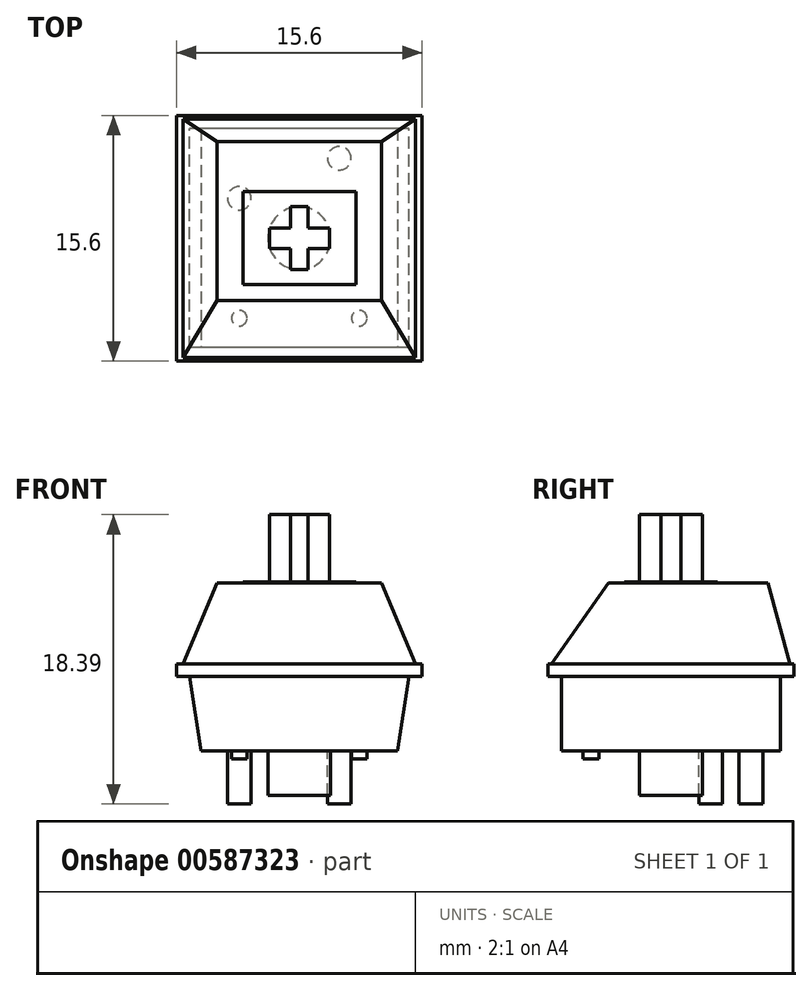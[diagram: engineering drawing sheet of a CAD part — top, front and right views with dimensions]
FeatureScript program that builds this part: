
annotation { "Feature Type Name" : "Feature", "Feature Type Description" : "" }
export const myFeature = defineFeature(function(context is Context, id is Id, definition is map)
    precondition{}
    {
        {
            var Q0;
            Q0=qCreatedBy(makeId("Top.planeOp"),FACE);
            var sketch = newSketch(context, id + "F0", { "sketchPlane" : qUnion([Q0])});
            skCircle(sketch, "E0", {"center": v(0, 0) * mm, "radius": 2 * mm});
            skCircle(sketch, "E1", {"center": v(-3.8, -5.08) * mm, "radius": 0.5 * mm});
            skCircle(sketch, "E2", {"center": v(3.81, -5.08) * mm, "radius": 0.5 * mm});
            skCircle(sketch, "E3", {"center": v(-3.81, 2.54) * mm, "radius": 0.75 * mm});
            skCircle(sketch, "E4", {"center": v(2.54, 5.08) * mm, "radius": 0.75 * mm});
            skLineSegment(sketch, "E5.bottom", {"start": v(6.97, -6.95) * mm, "end": v(-6.98, -6.95) * mm});
            skLineSegment(sketch, "E5.top", {"start": v(6.98, 6.95) * mm, "end": v(-6.97, 6.95) * mm});
            skLineSegment(sketch, "E5.left", {"start": v(6.97, -6.95) * mm, "end": v(6.98, 6.95) * mm});
            skLineSegment(sketch, "E5.right", {"start": v(-6.98, -6.95) * mm, "end": v(-6.97, 6.95) * mm});
            skSolve(sketch);
        }
        {
            var Q0;
            Q0=qCreatedBy(makeId("Top.planeOp"),FACE);
            var sketch = newSketch(context, id + "F1", { "sketchPlane" : qUnion([Q0])});
            skLineSegment(sketch, "E6", {"start": v(-0.55, 2) * mm, "end": v(0.55, 2) * mm});
            skLineSegment(sketch, "E7", {"start": v(0.55, 2) * mm, "end": v(0.55, 0.64) * mm});
            skLineSegment(sketch, "E8", {"start": v(0.55, 0.65) * mm, "end": v(1.9, 0.65) * mm});
            skLineSegment(sketch, "E9", {"start": v(1.9, 0.64) * mm, "end": v(1.9, -0.64) * mm});
            skLineSegment(sketch, "E10", {"start": v(1.9, -0.64) * mm, "end": v(0.55, -0.64) * mm});
            skLineSegment(sketch, "E11", {"start": v(0.55, -0.64) * mm, "end": v(0.55, -2) * mm});
            skLineSegment(sketch, "E12", {"start": v(0.55, -2) * mm, "end": v(-0.55, -2) * mm});
            skLineSegment(sketch, "E13", {"start": v(-0.55, -2) * mm, "end": v(-0.55, -0.65) * mm});
            skLineSegment(sketch, "E14", {"start": v(-0.55, -0.64) * mm, "end": v(-1.9, -0.64) * mm});
            skLineSegment(sketch, "E15", {"start": v(-1.9, -0.65) * mm, "end": v(-1.9, 0.65) * mm});
            skLineSegment(sketch, "E16", {"start": v(-1.9, 0.65) * mm, "end": v(-0.55, 0.65) * mm});
            skLineSegment(sketch, "E17", {"start": v(-0.55, 0.65) * mm, "end": v(-0.55, 2) * mm});
            skLineSegment(sketch, "E18", {"start": v(0, 2) * mm, "end": v(0, 0) * mm, "construction": true});
            skPoint(sketch, "E18.endSnap0", {"position": v(1.9, 0) * mm});
            skLineSegment(sketch, "E19.bottom", {"start": v(3.59, -2.95) * mm, "end": v(-3.59, -2.95) * mm});
            skLineSegment(sketch, "E19.top", {"start": v(3.59, 2.95) * mm, "end": v(-3.59, 2.95) * mm});
            skLineSegment(sketch, "E19.left", {"start": v(3.59, -2.95) * mm, "end": v(3.59, 2.95) * mm});
            skLineSegment(sketch, "E19.right", {"start": v(-3.59, -2.95) * mm, "end": v(-3.59, 2.95) * mm});
            skPoint(sketch, "E19.middle", {"position": v(0, 0) * mm});
            skLineSegment(sketch, "E20.bottom", {"start": v(5.24, 6.15) * mm, "end": v(-5.24, 6.15) * mm});
            skLineSegment(sketch, "E20.top", {"start": v(5.24, -3.95) * mm, "end": v(-5.24, -3.95) * mm});
            skLineSegment(sketch, "E20.left", {"start": v(5.24, 6.15) * mm, "end": v(5.24, -3.95) * mm});
            skLineSegment(sketch, "E20.right", {"start": v(-5.24, 6.15) * mm, "end": v(-5.24, -3.95) * mm});
            skPoint(sketch, "E20.middle", {"position": v(0, 1.1) * mm});
            skLineSegment(sketch, "E21.bottom", {"start": v(7.38, 7.58) * mm, "end": v(-7.38, 7.58) * mm});
            skLineSegment(sketch, "E21.top", {"start": v(7.37, -7.58) * mm, "end": v(-7.38, -7.57) * mm});
            skLineSegment(sketch, "E21.left", {"start": v(7.38, 7.57) * mm, "end": v(7.38, -7.58) * mm});
            skLineSegment(sketch, "E21.right", {"start": v(-7.37, 7.58) * mm, "end": v(-7.38, -7.58) * mm});
            skLineSegment(sketch, "E22.bottom", {"start": v(7.8, -7.8) * mm, "end": v(-7.8, -7.8) * mm});
            skLineSegment(sketch, "E22.top", {"start": v(7.8, 7.8) * mm, "end": v(-7.8, 7.8) * mm});
            skLineSegment(sketch, "E22.left", {"start": v(7.8, -7.8) * mm, "end": v(7.8, 7.8) * mm});
            skLineSegment(sketch, "E22.right", {"start": v(-7.8, -7.8) * mm, "end": v(-7.8, 7.8) * mm});
            skSolve(sketch);
        }
        {
            var Q0;
            Q0=qCreatedBy(makeId("Right.planeOp"),FACE);
            var sketch = newSketch(context, id + "F2", { "sketchPlane" : qUnion([Q0])});
            skLineSegment(sketch, "E23.bottom", {"start": v(-7.8, 0) * mm, "end": v(7.8, 0) * mm});
            skLineSegment(sketch, "E23.top", {"start": v(-7.8, 0.8) * mm, "end": v(7.8, 0.8) * mm});
            skLineSegment(sketch, "E23.left", {"start": v(-7.8, 0) * mm, "end": v(-7.8, 0.8) * mm});
            skLineSegment(sketch, "E23.right", {"start": v(7.8, 0) * mm, "end": v(7.8, 0.8) * mm});
            skLineSegment(sketch, "E24", {"start": v(-7.58, 0.8) * mm, "end": v(-3.95, 5.94) * mm});
            skLineSegment(sketch, "E25", {"start": v(-3.95, 5.94) * mm, "end": v(6.15, 5.94) * mm});
            skLineSegment(sketch, "E26", {"start": v(6.15, 5.94) * mm, "end": v(7.58, 0.8) * mm});
            skLineSegment(sketch, "E27", {"start": v(-2.95, 5.94) * mm, "end": v(-2.95, 6.02) * mm});
            skLineSegment(sketch, "E28", {"start": v(-2.95, 6.02) * mm, "end": v(2.95, 6.02) * mm});
            skLineSegment(sketch, "E29", {"start": v(2.95, 6.02) * mm, "end": v(2.95, 5.94) * mm});
            skLineSegment(sketch, "E30", {"start": v(-6.95, 0) * mm, "end": v(-6.95, -4.71) * mm});
            skLineSegment(sketch, "E31", {"start": v(-6.95, -4.71) * mm, "end": v(6.95, -4.71) * mm});
            skLineSegment(sketch, "E32", {"start": v(6.95, -4.71) * mm, "end": v(6.95, 0) * mm});
            skLineSegment(sketch, "E33", {"start": v(-2, 6.02) * mm, "end": v(-2, 10.29) * mm});
            skLineSegment(sketch, "E34", {"start": v(-2, 10.29) * mm, "end": v(2, 10.29) * mm});
            skLineSegment(sketch, "E35", {"start": v(2, 10.29) * mm, "end": v(2, 6.02) * mm});
            skLineSegment(sketch, "E36", {"start": v(-1.91, -4.71) * mm, "end": v(-1.91, -7.54) * mm});
            skLineSegment(sketch, "E37", {"start": v(-1.91, -7.54) * mm, "end": v(0, -7.54) * mm});
            skLineSegment(sketch, "E38", {"start": v(1.92, -7.54) * mm, "end": v(1.92, -4.71) * mm});
            skLineSegment(sketch, "E39", {"start": v(0, -7.54) * mm, "end": v(1.92, -7.54) * mm});
            skLineSegment(sketch, "E40", {"start": v(-7.8, 0.8) * mm, "end": v(-7.8, 5.94) * mm});
            skLineSegment(sketch, "E41", {"start": v(-7.8, 5.94) * mm, "end": v(-3.95, 5.94) * mm});
            skLineSegment(sketch, "E42", {"start": v(6.15, 5.94) * mm, "end": v(7.8, 5.94) * mm});
            skLineSegment(sketch, "E43", {"start": v(7.8, 5.94) * mm, "end": v(7.8, 0.8) * mm});
            skLineSegment(sketch, "E44", {"start": v(-5.58, -4.71) * mm, "end": v(-5.58, -5.23) * mm});
            skLineSegment(sketch, "E45", {"start": v(-5.58, -5.23) * mm, "end": v(-5.08, -5.23) * mm});
            skLineSegment(sketch, "E46", {"start": v(-4.58, -5.23) * mm, "end": v(-4.58, -4.71) * mm});
            skLineSegment(sketch, "E47", {"start": v(-5.08, -5.23) * mm, "end": v(-4.58, -5.23) * mm});
            skLineSegment(sketch, "E48", {"start": v(-5.58, -5.23) * mm, "end": v(-4.58, -5.23) * mm});
            skLineSegment(sketch, "E49", {"start": v(-5.58, -4.71) * mm, "end": v(-4.58, -4.71) * mm});
            skLineSegment(sketch, "E50", {"start": v(-6.95, -1.4) * mm, "end": v(6.95, -1.4) * mm, "construction": true});
            skSolve(sketch);
        }
        {
            var Q0;
            Q0=qCreatedBy(makeId("Front.planeOp"),FACE);
            var sketch = newSketch(context, id + "F3", { "sketchPlane" : qUnion([Q0])});
            skLineSegment(sketch, "E51.bottom", {"start": v(-7.8, 0.8) * mm, "end": v(7.8, 0.8) * mm});
            skLineSegment(sketch, "E51.top", {"start": v(-7.8, 0) * mm, "end": v(7.8, 0) * mm});
            skLineSegment(sketch, "E51.left", {"start": v(-7.8, 0.8) * mm, "end": v(-7.8, 0) * mm});
            skLineSegment(sketch, "E51.right", {"start": v(7.8, 0.8) * mm, "end": v(7.8, 0) * mm});
            skLineSegment(sketch, "E52", {"start": v(-7.38, 0.8) * mm, "end": v(-5.24, 5.94) * mm});
            skLineSegment(sketch, "E53", {"start": v(-5.24, 5.94) * mm, "end": v(5.24, 5.94) * mm});
            skLineSegment(sketch, "E54", {"start": v(5.24, 5.94) * mm, "end": v(7.37, 0.8) * mm});
            skLineSegment(sketch, "E55", {"start": v(-3.59, 5.94) * mm, "end": v(-3.59, 6.02) * mm});
            skLineSegment(sketch, "E56", {"start": v(-3.59, 6.02) * mm, "end": v(3.59, 6.02) * mm});
            skLineSegment(sketch, "E57", {"start": v(3.59, 6.02) * mm, "end": v(3.59, 5.94) * mm});
            skLineSegment(sketch, "E58", {"start": v(-1.9, 6.02) * mm, "end": v(-1.9, 10.29) * mm});
            skLineSegment(sketch, "E59", {"start": v(-1.9, 10.29) * mm, "end": v(1.9, 10.29) * mm});
            skLineSegment(sketch, "E60", {"start": v(1.9, 10.29) * mm, "end": v(1.9, 6.02) * mm});
            skLineSegment(sketch, "E61", {"start": v(-6.98, 0) * mm, "end": v(-6.23, -4.71) * mm});
            skLineSegment(sketch, "E62", {"start": v(-6.23, -4.71) * mm, "end": v(0, -4.71) * mm});
            skLineSegment(sketch, "E63", {"start": v(6.23, -4.71) * mm, "end": v(6.98, 0) * mm});
            skLineSegment(sketch, "E64", {"start": v(-1.92, -4.71) * mm, "end": v(-1.91, -7.54) * mm});
            skLineSegment(sketch, "E65", {"start": v(-1.91, -7.54) * mm, "end": v(0, -7.54) * mm});
            skLineSegment(sketch, "E66", {"start": v(1.91, -7.54) * mm, "end": v(1.91, -4.71) * mm});
            skLineSegment(sketch, "E67", {"start": v(0, -7.54) * mm, "end": v(1.91, -7.54) * mm});
            skLineSegment(sketch, "E68", {"start": v(0, -4.71) * mm, "end": v(6.23, -4.7) * mm});
            skLineSegment(sketch, "E69", {"start": v(-5.24, 5.94) * mm, "end": v(-7.8, 5.94) * mm});
            skLineSegment(sketch, "E70", {"start": v(-7.8, 5.94) * mm, "end": v(-7.8, 0.8) * mm});
            skLineSegment(sketch, "E71", {"start": v(5.24, 5.94) * mm, "end": v(7.8, 5.94) * mm});
            skLineSegment(sketch, "E72", {"start": v(7.8, 5.94) * mm, "end": v(7.8, 0.8) * mm});
            skLineSegment(sketch, "E73", {"start": v(-7.8, 0) * mm, "end": v(-7.8, -4.71) * mm});
            skLineSegment(sketch, "E74", {"start": v(-7.8, -4.71) * mm, "end": v(-6.23, -4.71) * mm});
            skLineSegment(sketch, "E75", {"start": v(6.23, -4.71) * mm, "end": v(7.8, -4.71) * mm});
            skLineSegment(sketch, "E76", {"start": v(7.8, -4.71) * mm, "end": v(7.8, 0) * mm});
            skLineSegment(sketch, "E77", {"start": v(-6.75, -1.4) * mm, "end": v(6.75, -1.4) * mm, "construction": true});
            skLineSegment(sketch, "E78", {"start": v(-4.56, -4.71) * mm, "end": v(-4.56, -8.1) * mm});
            skLineSegment(sketch, "E79", {"start": v(-4.56, -8.1) * mm, "end": v(-3.06, -8.1) * mm});
            skLineSegment(sketch, "E80", {"start": v(-3.06, -8.1) * mm, "end": v(-3.06, -4.71) * mm});
            skLineSegment(sketch, "E81", {"start": v(-4.56, -8.1) * mm, "end": v(-3.8, -8.1) * mm, "construction": true});
            skLineSegment(sketch, "E82", {"start": v(-3.8, -8.1) * mm, "end": v(-3.06, -8.1) * mm, "construction": true});
            skSolve(sketch);
        }
        {
            var Q0;
            Q0=makeQuery(id+"F1.imprint","IMPRINT",FACE,{"disambiguationData":[TD([[makeQuery(id+"F1.imprint","IMPRINT",EDGE,{"derivedFrom":sQuery(id+"F1.wireOp",EDGE,"E6")}),-1.0]])]});
            var Q1;
            Q1=sQuery(id+"F3.wireOp",VERTEX,"E59.end");
            extrude(context, id + "F4", {"entities" : qUnion([Q0]), "endBound" : BoundingType.UP_TO_VERTEX, "depth" : 25 * mm, "endBoundEntityVertex" : qUnion([Q1]), "offsetDistance" : 25 * mm});
        }
        {
            var Q0;
            Q0=makeQuery(id+"F1.imprint","IMPRINT",FACE,{"disambiguationData":[TD([[makeQuery(id+"F1.imprint","IMPRINT",EDGE,{"derivedFrom":sQuery(id+"F1.wireOp",EDGE,"E6")}),1.0]])]});
            var Q1;
            Q1=sQuery(id+"F2.wireOp",VERTEX,"E27.end");
            extrude(context, id + "F5", {"entities" : qUnion([Q0]), "operationType" : NewBodyOperationType.ADD, "endBound" : BoundingType.UP_TO_VERTEX, "depth" : 25 * mm, "endBoundEntityVertex" : qUnion([Q1]), "offsetDistance" : 25 * mm});
        }
        {
            var Q0;
            Q0=makeQuery(id+"F1.imprint","IMPRINT",FACE,{"disambiguationData":[TD([[makeQuery(id+"F1.imprint","IMPRINT",EDGE,{"derivedFrom":sQuery(id+"F1.wireOp",EDGE,"E19.bottom")}),1.0]])]});
            var Q1;
            Q1=makeQuery(id+"F1.imprint","IMPRINT",FACE,{"disambiguationData":[TD([[makeQuery(id+"F1.imprint","IMPRINT",EDGE,{"derivedFrom":sQuery(id+"F1.wireOp",EDGE,"E20.bottom")}),-1.0]])]});
            var Q2;
            Q2=sQuery(id+"F2.wireOp",VERTEX,"E24.end");
            extrude(context, id + "F6", {"entities" : qUnion([Q0, Q1]), "operationType" : NewBodyOperationType.ADD, "endBound" : BoundingType.UP_TO_VERTEX, "depth" : 25 * mm, "endBoundEntityVertex" : qUnion([Q2]), "offsetDistance" : 25 * mm});
        }
        {
            var Q0;
            Q0=makeQuery(id+"F1.imprint","IMPRINT",FACE,{"disambiguationData":[TD([[makeQuery(id+"F1.imprint","IMPRINT",EDGE,{"derivedFrom":sQuery(id+"F1.wireOp",EDGE,"E21.bottom")}),-1.0]])]});
            var Q1;
            Q1=sQuery(id+"F2.wireOp",VERTEX,"E23.top.start");
            extrude(context, id + "F7", {"entities" : qUnion([Q0]), "operationType" : NewBodyOperationType.ADD, "endBound" : BoundingType.UP_TO_VERTEX, "depth" : 25 * mm, "endBoundEntityVertex" : qUnion([Q1]), "offsetDistance" : 25 * mm});
        }
        {
            var Q0;
            {var subQ2=sQuery(id+"F2.wireOp",EDGE,"E24");Q0=makeQuery(id+"F2.imprint","IMPRINT",FACE,{"disambiguationData":[TD([[makeQuery(id+"F2.imprint","IMPRINT",EDGE,{"derivedFrom":subQ2}),1.0]])]});}
            var Q1;
            {var subQ2=sQuery(id+"F2.wireOp",EDGE,"E26");Q1=makeQuery(id+"F2.imprint","IMPRINT",FACE,{"disambiguationData":[TD([[makeQuery(id+"F2.imprint","IMPRINT",EDGE,{"derivedFrom":subQ2}),1.0]])]});}
            extrude(context, id + "F8", {"entities" : qUnion([Q0, Q1]), "operationType" : NewBodyOperationType.REMOVE, "endBound" : BoundingType.THROUGH_ALL, "oppositeDirection" : true, "depth" : 25 * mm, "offsetDistance" : 25 * mm, "hasSecondDirection" : true, "secondDirectionBound" : BoundingType.THROUGH_ALL, "secondDirectionOppositeDirection" : false, "secondDirectionDepth" : 25 * mm});
        }
        {
            var Q0;
            {var subQ2=sQuery(id+"F3.wireOp",EDGE,"E52");Q0=makeQuery(id+"F3.imprint","IMPRINT",FACE,{"disambiguationData":[TD([[makeQuery(id+"F3.imprint","IMPRINT",EDGE,{"derivedFrom":subQ2}),1.0]])]});}
            var Q1;
            {var subQ2=sQuery(id+"F3.wireOp",EDGE,"E54");Q1=makeQuery(id+"F3.imprint","IMPRINT",FACE,{"disambiguationData":[TD([[makeQuery(id+"F3.imprint","IMPRINT",EDGE,{"derivedFrom":subQ2}),1.0]])]});}
            extrude(context, id + "F9", {"entities" : qUnion([Q0, Q1]), "operationType" : NewBodyOperationType.REMOVE, "endBound" : BoundingType.THROUGH_ALL, "oppositeDirection" : true, "depth" : 25 * mm, "offsetDistance" : 25 * mm, "hasSecondDirection" : true, "secondDirectionBound" : BoundingType.THROUGH_ALL, "secondDirectionOppositeDirection" : false, "secondDirectionDepth" : 25 * mm});
        }
        {
            var Q0;
            Q0=makeQuery(id+"F0.imprint","IMPRINT",FACE,{"disambiguationData":[TD([[makeQuery(id+"F0.imprint","IMPRINT",EDGE,{"derivedFrom":sQuery(id+"F0.wireOp",EDGE,"E0")}),-1.0]])]});
            var Q1;
            Q1=sQuery(id+"F3.wireOp",VERTEX,"E61.end");
            extrude(context, id + "F10", {"entities" : qUnion([Q0]), "operationType" : NewBodyOperationType.ADD, "endBound" : BoundingType.UP_TO_VERTEX, "oppositeDirection" : true, "depth" : 25 * mm, "endBoundEntityVertex" : qUnion([Q1]), "offsetDistance" : 25 * mm});
        }
        {
            var Q0;
            Q0=makeQuery(id+"F0.imprint","IMPRINT",FACE,{"disambiguationData":[TD([[makeQuery(id+"F0.imprint","IMPRINT",EDGE,{"derivedFrom":sQuery(id+"F0.wireOp",EDGE,"E0")}),1.0]])]});
            var Q1;
            Q1=sQuery(id+"F2.wireOp",VERTEX,"E37.end");
            extrude(context, id + "F11", {"entities" : qUnion([Q0]), "operationType" : NewBodyOperationType.ADD, "endBound" : BoundingType.UP_TO_VERTEX, "oppositeDirection" : true, "depth" : 25 * mm, "endBoundEntityVertex" : qUnion([Q1]), "offsetDistance" : 25 * mm});
        }
        {
            var Q0;
            Q0=makeQuery(id+"F0.imprint","IMPRINT",FACE,{"disambiguationData":[TD([[makeQuery(id+"F0.imprint","IMPRINT",EDGE,{"derivedFrom":sQuery(id+"F0.wireOp",EDGE,"E3")}),1.0]])]});
            var Q1;
            Q1=makeQuery(id+"F0.imprint","IMPRINT",FACE,{"disambiguationData":[TD([[makeQuery(id+"F0.imprint","IMPRINT",EDGE,{"derivedFrom":sQuery(id+"F0.wireOp",EDGE,"E4")}),1.0]])]});
            var Q2;
            Q2=sQuery(id+"F3.wireOp",VERTEX,"E81.end");
            extrude(context, id + "F12", {"entities" : qUnion([Q0, Q1]), "operationType" : NewBodyOperationType.ADD, "endBound" : BoundingType.UP_TO_VERTEX, "oppositeDirection" : true, "depth" : 25 * mm, "endBoundEntityVertex" : qUnion([Q2]), "offsetDistance" : 25 * mm});
        }
        {
            var Q0;
            Q0=makeQuery(id+"F0.imprint","IMPRINT",FACE,{"disambiguationData":[TD([[makeQuery(id+"F0.imprint","IMPRINT",EDGE,{"derivedFrom":sQuery(id+"F0.wireOp",EDGE,"E2")}),1.0]])]});
            var Q1;
            Q1=makeQuery(id+"F0.imprint","IMPRINT",FACE,{"disambiguationData":[TD([[makeQuery(id+"F0.imprint","IMPRINT",EDGE,{"derivedFrom":sQuery(id+"F0.wireOp",EDGE,"E1")}),1.0]])]});
            var Q2;
            Q2=sQuery(id+"F0.wireOp",EDGE,"E2");
            var Q3;
            Q3=sQuery(id+"F0.wireOp",EDGE,"E1");
            var Q4;
            Q4=sQuery(id+"F2.wireOp",VERTEX,"E45.end");
            extrude(context, id + "F13", {"entities" : qUnion([Q0, Q1]), "operationType" : NewBodyOperationType.ADD, "surfaceOperationType" : NewSurfaceOperationType.ADD, "surfaceEntities" : qUnion([Q2, Q3]), "endBound" : BoundingType.UP_TO_VERTEX, "oppositeDirection" : true, "depth" : 25 * mm, "endBoundEntityVertex" : qUnion([Q4]), "offsetDistance" : 25 * mm});
        }
        {
            var Q0;
            {var subQ2=sQuery(id+"F3.wireOp",EDGE,"E61");Q0=makeQuery(id+"F3.imprint","IMPRINT",FACE,{"disambiguationData":[TD([[makeQuery(id+"F3.imprint","IMPRINT",EDGE,{"derivedFrom":subQ2}),-1.0]])]});}
            var Q1;
            {var subQ2=sQuery(id+"F3.wireOp",EDGE,"E63");Q1=makeQuery(id+"F3.imprint","IMPRINT",FACE,{"disambiguationData":[TD([[makeQuery(id+"F3.imprint","IMPRINT",EDGE,{"derivedFrom":subQ2}),-1.0]])]});}
            extrude(context, id + "F14", {"entities" : qUnion([Q0, Q1]), "operationType" : NewBodyOperationType.REMOVE, "endBound" : BoundingType.THROUGH_ALL, "oppositeDirection" : true, "depth" : 25 * mm, "offsetDistance" : 25 * mm, "hasSecondDirection" : true, "secondDirectionBound" : BoundingType.THROUGH_ALL, "secondDirectionOppositeDirection" : false, "secondDirectionDepth" : 25 * mm});
        }
    });
